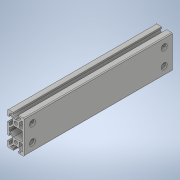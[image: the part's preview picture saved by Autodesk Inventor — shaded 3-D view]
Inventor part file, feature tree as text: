
AUTODESK INVENTOR PART (.ipt)
format: ipt  version: 2022 (Build 260153000, 153)  size: 400,896 bytes
history: native  units: mm
features: other x7, sketch x7, hole x6, extrude x1, pattern_linear x1
ambient origin geometry x8: Origin, YZ Plane, XZ Plane, XY Plane, X Axis, Y Axis, Z Axis, Center Point
bodies: Solid1 (feature_tree)
feature tree (22):
  extrude  "Extrusion1"  Depth=10.0mm TaperAngle=0.0deg
  hole  "Hole1"  [1 undecoded]
  pattern_linear  "Rectangular Pattern1"  Spacing1=10.0mm  [1 undecoded]
  hole  "Hole2"  [1 undecoded]
  hole  "Hole3"  [1 undecoded]
  hole  "Hole6"  [1 undecoded]
  hole  "Hole7"  [1 undecoded]
  other  "C1_XY"
  other  "C1_YZ"
  other  "C1_ZX"
  other  "C1_X"
  other  "C1_Y"
  other  "C1_Z"
  other  "C1_Center"
  hole  "穴12"  [1 undecoded]
  sketch  "Sketch_63"  dims[d50=7.35mm d51=6.0mm d52=4.0mm d53=2.0mm d54=90.0deg d55=20.0mm d56=0.0mm d64=0.0mm d100=10.0mm d101=3.0mm d102=20.0mm d103=10.0mm d104=170.0mm d105=9.0mm d106=6.0mm d107=4.0mm d108=2.0mm d109=90.0deg d110=6.0mm d111=20.594885mm d119=1.0mm d120=1.0mm d121=1.0mm d122=0.15mm d123=0.25mm d124=0.375mm d125=14.3117mm d126=0.75mm d127=20.594885mm d128=0.0625mm d129=0.75mm d130=0.375mm]
  sketch  "Sketch2"  dims[d0=180.0mm d1=0.0mm]
  sketch  "Sketch3"  dims[d2=4.2mm d3=6.0mm d4=4.0mm d5=2.0mm d6=90.0deg d7=180.0mm d8=0.0mm d9=20.0mm d11=20.0mm d12=10.0mm d14=0.0mm]
  sketch  "Sketch4"  dims[d15=7.35mm d16=6.0mm d17=4.0mm d18=2.0mm d19=90.0deg d20=20.0mm d21=0.0mm]
  sketch  "Sketch7"  dims[d22=7.35mm d23=6.0mm d24=4.0mm d25=2.0mm d26=90.0deg d27=20.0mm d28=0.0mm]
  sketch  "Sketch8"  dims[d43=7.35mm d44=6.0mm d45=4.0mm d46=2.0mm d47=90.0deg d48=20.0mm d49=0.0mm]
  sketch  "スケッチ12"
note: 7 required parameter values undecoded (feature->parameter linkage not recoverable at this tier; creation-order binding heuristic only, values carry confidence <= 0.55)
